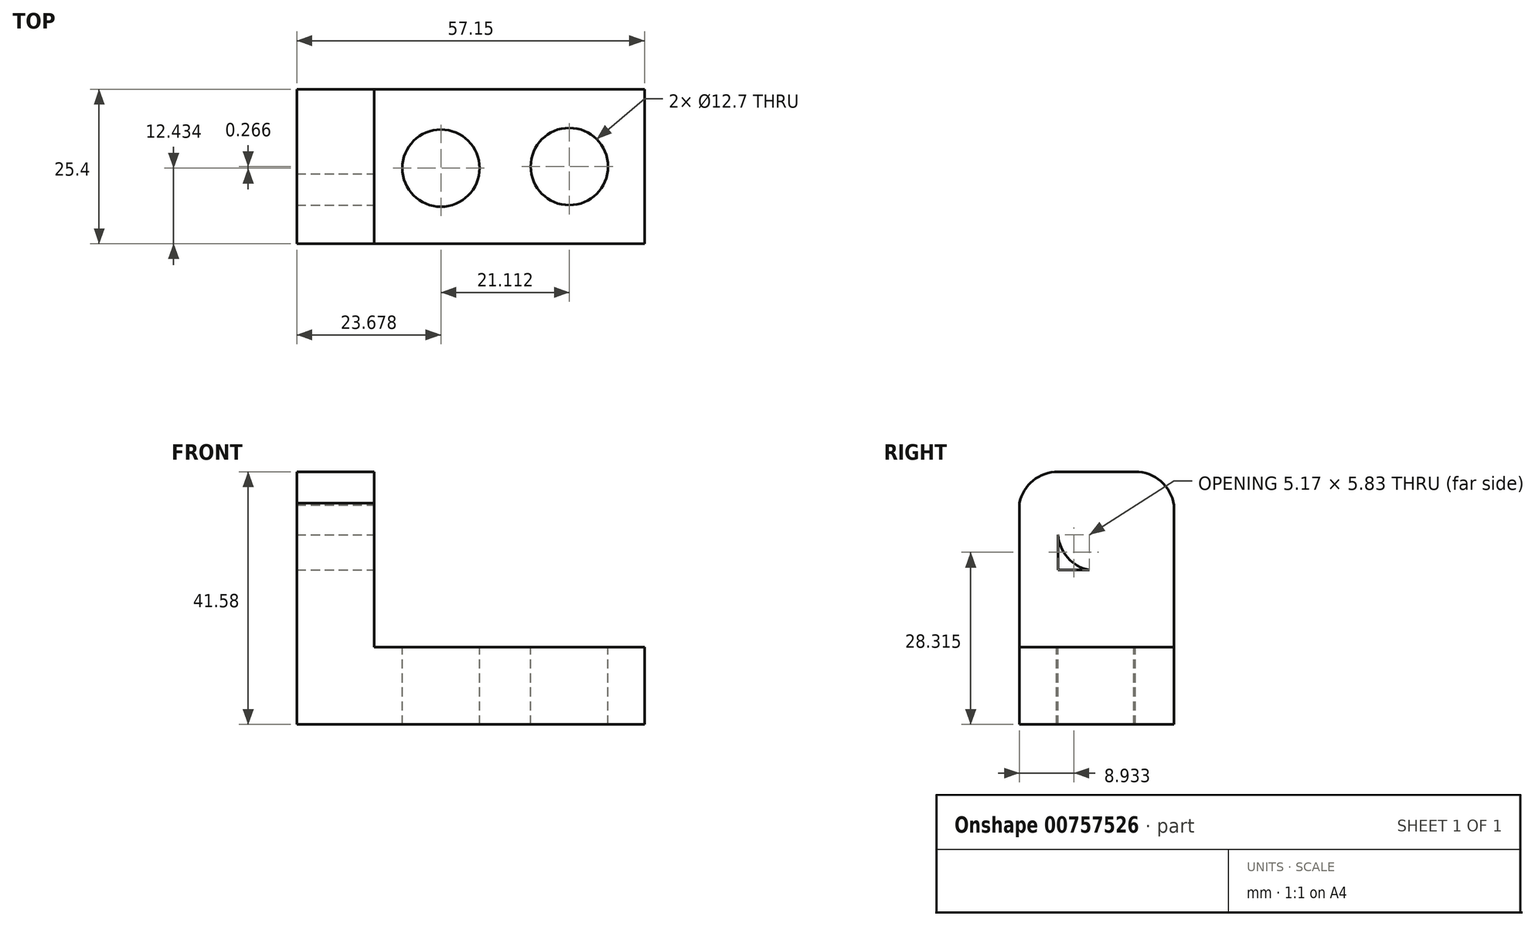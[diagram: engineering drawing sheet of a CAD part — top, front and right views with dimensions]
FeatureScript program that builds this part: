
annotation { "Feature Type Name" : "Feature", "Feature Type Description" : "" }
export const myFeature = defineFeature(function(context is Context, id is Id, definition is map)
    precondition{}
    {
        {
            var Q0;
            Q0=qCreatedBy(makeId("Front.planeOp"),FACE);
            var sketch = newSketch(context, id + "F0", { "sketchPlane" : qUnion([Q0])});
            skLineSegment(sketch, "E0", {"start": v(0, 0) * mm, "end": v(-57.15, 0) * mm});
            skLineSegment(sketch, "E1", {"start": v(-57.15, 0) * mm, "end": v(-57.15, 41.58) * mm});
            skLineSegment(sketch, "E2", {"start": v(-57.15, 41.58) * mm, "end": v(0, 41.58) * mm});
            skLineSegment(sketch, "E3", {"start": v(0, 41.58) * mm, "end": v(0, 0) * mm});
            skSolve(sketch);
        }
        {
            var Q0;
            Q0 = qSketchRegion(id + "F0", true);
            extrude(context, id + "F1", {"entities" : qUnion([Q0]), "depth" : 25.4 * mm, "offsetDistance" : 25.4 * mm});
        }
        {
            var Q0;
            Q0=makeQuery(id+"F1.opExtrude","CAP_FACE",FACE,{"disambiguationData":[OSD([sQuery(id+"F0.wireOp",EDGE,"E0"),sQuery(id+"F0.wireOp",EDGE,"E1"),sQuery(id+"F0.wireOp",EDGE,"E2"),sQuery(id+"F0.wireOp",EDGE,"E3")])],"isStart":false});
            var sketch = newSketch(context, id + "F2", { "sketchPlane" : qUnion([Q0])});
            skLineSegment(sketch, "E4", {"start": v(-44.45, 41.58) * mm, "end": v(-44.45, 12.7) * mm});
            skLineSegment(sketch, "E5", {"start": v(-44.45, 12.7) * mm, "end": v(0, 12.7) * mm});
            skSolve(sketch);
        }
        {
            var Q0;
            {var subQ0=sQuery(id+"F2.wireOp",EDGE,"E4");Q0=makeQuery(id+"F2.imprint","IMPRINT",FACE,{"disambiguationData":[TD([[makeQuery(id+"F2.imprint","IMPRINT",EDGE,{"derivedFrom":subQ0}),1.0]])]});}
            extrude(context, id + "F3", {"entities" : qUnion([Q0]), "operationType" : NewBodyOperationType.REMOVE, "endBound" : BoundingType.THROUGH_ALL, "oppositeDirection" : true, "depth" : 25.4 * mm, "offsetDistance" : 25.4 * mm});
        }
        {
            var Q0;
            Q0=makeQuery(id+"F3.boolean.opBoolean","COPY",FACE,{"derivedFrom":makeQuery(id+"F3.opExtrude","SWEPT_FACE",FACE,{"disambiguationData":[OSD([sQuery(id+"F2.wireOp",EDGE,"E4")])]})});
            var sketch = newSketch(context, id + "F4", { "sketchPlane" : qUnion([Q0])});
            skLineSegment(sketch, "E6", {"start": v(-19.05, 41.58) * mm, "end": v(-19.05, 25.4) * mm});
            skLineSegment(sketch, "E7", {"start": v(-19.05, 25.4) * mm, "end": v(-6.35, 25.4) * mm});
            skLineSegment(sketch, "E8", {"start": v(-6.35, 25.4) * mm, "end": v(-6.35, 41.58) * mm});
            skArc(sketch, "E9", {"start": v(-19.05, 32.06) * mm, "mid": v(-12.9, 25.3) * mm, "end": v(-6.35, 31.66) * mm});
            skSolve(sketch);
        }
        {
            var Q0;
            {var subQ3=sQuery(id+"F4.wireOp",EDGE,"E9");var subQ5=sQuery(id+"F4.wireOp",EDGE,"E6");var subQ10=makeQuery(id+"F4.imprint","INTERSECT",VERTEX,{"disambiguationData":[OD(0.0)],"derivedFrom":[subQ5,subQ3]});Q0=makeQuery(id+"F4.imprint","IMPRINT",FACE,{"disambiguationData":[TD([[makeQuery(id+"F4.imprint","IMPRINT",EDGE,{"disambiguationData":[TD([[subQ10,-1.0]])],"derivedFrom":subQ5}),1.0]])]});}
            extrude(context, id + "F5", {"entities" : qUnion([Q0]), "operationType" : NewBodyOperationType.REMOVE, "endBound" : BoundingType.THROUGH_ALL, "oppositeDirection" : true, "depth" : 25.4 * mm, "offsetDistance" : 25.4 * mm});
        }
        {
            var Q0;
            Q0=makeQuery(id+"F3.boolean.opBoolean","COPY",FACE,{"derivedFrom":makeQuery(id+"F3.opExtrude","SWEPT_FACE",FACE,{"disambiguationData":[OSD([sQuery(id+"F2.wireOp",EDGE,"E4")])]})});
            var sketch = newSketch(context, id + "F6", { "sketchPlane" : qUnion([Q0])});
            skArc(sketch, "E10", {"start": v(-19.05, 41.58) * mm, "mid": v(-23.15, 40.12) * mm, "end": v(-25.4, 36.4) * mm});
            skPoint(sketch, "E10.endSnap0", {"position": v(-19.05, 36.4) * mm});
            skArc(sketch, "E11", {"start": v(0, 36.08) * mm, "mid": v(-2.15, 40.01) * mm, "end": v(-6.35, 41.58) * mm});
            skSolve(sketch);
        }
        {
            var Q0;
            {var subQ0=sQuery(id+"F6.wireOp",EDGE,"E10");Q0=makeQuery(id+"F6.imprint","IMPRINT",FACE,{"disambiguationData":[TD([[makeQuery(id+"F6.imprint","IMPRINT",EDGE,{"derivedFrom":subQ0}),-1.0]])]});}
            var Q1;
            {var subQ0=sQuery(id+"F6.wireOp",EDGE,"E11");Q1=makeQuery(id+"F6.imprint","IMPRINT",FACE,{"disambiguationData":[TD([[makeQuery(id+"F6.imprint","IMPRINT",EDGE,{"derivedFrom":subQ0}),-1.0]])]});}
            extrude(context, id + "F7", {"entities" : qUnion([Q0, Q1]), "operationType" : NewBodyOperationType.REMOVE, "endBound" : BoundingType.THROUGH_ALL, "oppositeDirection" : true, "depth" : 25.4 * mm, "offsetDistance" : 25.4 * mm});
        }
        {
            var Q0;
            Q0=makeQuery(id+"F3.boolean.opBoolean","COPY",FACE,{"derivedFrom":makeQuery(id+"F3.opExtrude","SWEPT_FACE",FACE,{"disambiguationData":[OSD([sQuery(id+"F2.wireOp",EDGE,"E5")])]})});
            var sketch = newSketch(context, id + "F8", { "sketchPlane" : qUnion([Q0])});
            skArc(sketch, "E12", {"start": v(-14.57, -25.4) * mm, "mid": v(0.53, -12.7) * mm, "end": v(-14.57, 0) * mm});
            skCircle(sketch, "E13", {"center": v(-33.47, -12.97) * mm, "radius": 6.35 * mm});
            skCircle(sketch, "E14", {"center": v(-12.36, -12.7) * mm, "radius": 6.35 * mm});
            skSolve(sketch);
        }
        {
            var Q0;
            Q0=makeQuery(id+"F8.imprint","IMPRINT",FACE,{"disambiguationData":[TD([[makeQuery(id+"F8.imprint","IMPRINT",EDGE,{"derivedFrom":sQuery(id+"F8.wireOp",EDGE,"E13")}),1.0]])]});
            var Q1;
            Q1=makeQuery(id+"F8.imprint","IMPRINT",FACE,{"disambiguationData":[TD([[makeQuery(id+"F8.imprint","IMPRINT",EDGE,{"derivedFrom":sQuery(id+"F8.wireOp",EDGE,"E14")}),1.0]])]});
            var Q2;
            {var subQ0=sQuery(id+"F8.wireOp",EDGE,"E12");var subQ1=sQuery(id+"F2.wireOp",EDGE,"E5");var subQ2=sQuery(id+"F0.wireOp",EDGE,"E3");var subQ3=makeQuery(id+"F3.boolean.opBoolean","COPY",EDGE,{"derivedFrom":makeQuery(id+"F3.opExtrude","SWEPT_EDGE",EDGE,{"disambiguationData":[OSD([subQ2,subQ1])]})});var subQ4=makeQuery(id+"F8.imprint","INTERSECT",VERTEX,{"disambiguationData":[OD(1.0)],"derivedFrom":[subQ3,subQ0]});Q2=makeQuery(id+"F8.imprint","IMPRINT",FACE,{"disambiguationData":[TD([[makeQuery(id+"F8.imprint","IMPRINT",EDGE,{"disambiguationData":[TD([[subQ4,-1.0]])],"derivedFrom":subQ0}),-1.0]])]});}
            var Q3;
            {var subQ0=sQuery(id+"F8.wireOp",EDGE,"E12");var subQ1=sQuery(id+"F2.wireOp",EDGE,"E5");var subQ2=makeQuery(id+"F3.boolean.opBoolean","COPY",EDGE,{"derivedFrom":makeQuery(id+"F3.opExtrude","CAP_EDGE",EDGE,{"disambiguationData":[OSD([subQ1])],"isStart":true})});var subQ3=makeQuery(id+"F8.imprint","INTERSECT",VERTEX,{"disambiguationData":[OD(1.0)],"derivedFrom":[subQ2,subQ0]});Q3=makeQuery(id+"F8.imprint","IMPRINT",FACE,{"disambiguationData":[TD([[makeQuery(id+"F8.imprint","IMPRINT",EDGE,{"disambiguationData":[TD([[subQ3,-1.0]])],"derivedFrom":subQ0}),-1.0]])]});}
            extrude(context, id + "F9", {"entities" : qUnion([Q0, Q1, Q2, Q3]), "operationType" : NewBodyOperationType.REMOVE, "endBound" : BoundingType.THROUGH_ALL, "oppositeDirection" : true, "depth" : 25.4 * mm, "offsetDistance" : 25.4 * mm});
        }
    });
